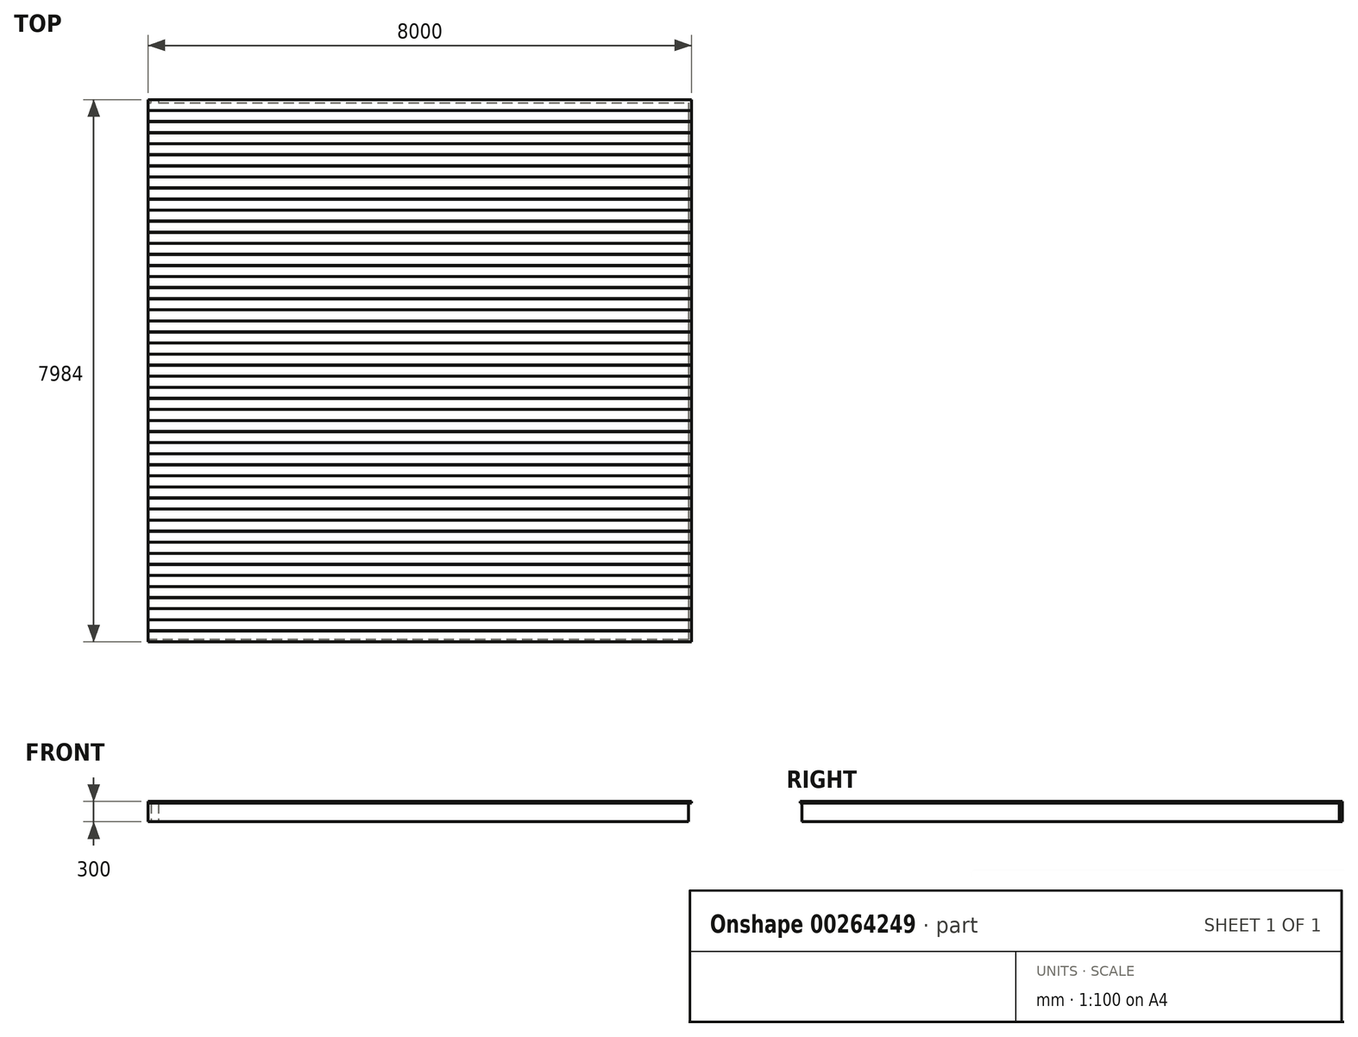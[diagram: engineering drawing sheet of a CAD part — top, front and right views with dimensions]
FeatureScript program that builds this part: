
annotation { "Feature Type Name" : "Feature", "Feature Type Description" : "" }
export const myFeature = defineFeature(function(context is Context, id is Id, definition is map)
    precondition{}
    {
        {
            var Q0;
            Q0=qCreatedBy(makeId("Top.planeOp"),FACE);
            var sketch = newSketch(context, id + "F0", { "sketchPlane" : qUnion([Q0])});
            skLineSegment(sketch, "E0.bottom", {"start": v(0, 0) * mm, "end": v(8000, 0) * mm});
            skLineSegment(sketch, "E0.top", {"start": v(0, -8000) * mm, "end": v(8000, -8000) * mm});
            skLineSegment(sketch, "E0.left", {"start": v(0, 0) * mm, "end": v(0, -8000) * mm});
            skLineSegment(sketch, "E0.right", {"start": v(8000, 0) * mm, "end": v(8000, -8000) * mm});
            skLineSegment(sketch, "E1.bottom", {"start": v(8000, 0) * mm, "end": v(7955, 0) * mm});
            skLineSegment(sketch, "E1.top", {"start": v(8000, -8000) * mm, "end": v(7955, -8000) * mm});
            skLineSegment(sketch, "E1.right", {"start": v(7955, 0) * mm, "end": v(7955, -8000) * mm});
            skLineSegment(sketch, "E2.bottom", {"start": v(7955, -8000) * mm, "end": v(0, -8000) * mm});
            skLineSegment(sketch, "E2.top", {"start": v(7955, -7955) * mm, "end": v(0, -7955) * mm});
            skLineSegment(sketch, "E2.left", {"start": v(7955, -8000) * mm, "end": v(7955, -7955) * mm});
            skLineSegment(sketch, "E2.right", {"start": v(0, -8000) * mm, "end": v(0, -7955) * mm});
            skLineSegment(sketch, "E3.bottom", {"start": v(0, -8000) * mm, "end": v(45, -8000) * mm});
            skLineSegment(sketch, "E3.top", {"start": v(0, 0) * mm, "end": v(45, 0) * mm});
            skLineSegment(sketch, "E3.left", {"start": v(0, -8000) * mm, "end": v(0, 0) * mm});
            skLineSegment(sketch, "E3.right", {"start": v(45, -8000) * mm, "end": v(45, 0) * mm});
            skLineSegment(sketch, "E4.top", {"start": v(0, -45) * mm, "end": v(8000, -45) * mm});
            skLineSegment(sketch, "E4.left", {"start": v(0, 0) * mm, "end": v(0, -45) * mm});
            skLineSegment(sketch, "E4.right", {"start": v(8000, 0) * mm, "end": v(8000, -45) * mm});
            skLineSegment(sketch, "E5.1.0.0", {"start": v(7400, 0) * mm, "end": v(7400, -8000) * mm});
            skLineSegment(sketch, "E5.1.0.1", {"start": v(7355, 0) * mm, "end": v(7355, -8000) * mm});
            skLineSegment(sketch, "E5.1.0.2", {"start": v(7400, 0) * mm, "end": v(7400, -8000) * mm});
            skLineSegment(sketch, "E5.1.0.3", {"start": v(7355, -8000) * mm, "end": v(7355, -7955) * mm});
            skLineSegment(sketch, "E5.1.0.4", {"start": v(7400, -8000) * mm, "end": v(7355, -8000) * mm});
            skLineSegment(sketch, "E5.1.0.5", {"start": v(7400, 0) * mm, "end": v(7355, 0) * mm});
            skLineSegment(sketch, "E5.1.0.6", {"start": v(7400, 0) * mm, "end": v(7400, -45) * mm});
            skLineSegment(sketch, "E5.2.0.0", {"start": v(6800, 0) * mm, "end": v(6800, -8000) * mm});
            skLineSegment(sketch, "E5.2.0.1", {"start": v(6755, 0) * mm, "end": v(6755, -8000) * mm});
            skLineSegment(sketch, "E5.2.0.2", {"start": v(6800, 0) * mm, "end": v(6800, -8000) * mm});
            skLineSegment(sketch, "E5.2.0.3", {"start": v(6755, -8000) * mm, "end": v(6755, -7955) * mm});
            skLineSegment(sketch, "E5.2.0.4", {"start": v(6800, -8000) * mm, "end": v(6755, -8000) * mm});
            skLineSegment(sketch, "E5.2.0.5", {"start": v(6800, 0) * mm, "end": v(6755, 0) * mm});
            skLineSegment(sketch, "E5.2.0.6", {"start": v(6800, 0) * mm, "end": v(6800, -45) * mm});
            skLineSegment(sketch, "E5.3.0.0", {"start": v(6200, 0) * mm, "end": v(6200, -8000) * mm});
            skLineSegment(sketch, "E5.3.0.1", {"start": v(6155, 0) * mm, "end": v(6155, -8000) * mm});
            skLineSegment(sketch, "E5.3.0.2", {"start": v(6200, 0) * mm, "end": v(6200, -8000) * mm});
            skLineSegment(sketch, "E5.3.0.3", {"start": v(6155, -8000) * mm, "end": v(6155, -7955) * mm});
            skLineSegment(sketch, "E5.3.0.4", {"start": v(6200, -8000) * mm, "end": v(6155, -8000) * mm});
            skLineSegment(sketch, "E5.3.0.5", {"start": v(6200, 0) * mm, "end": v(6155, 0) * mm});
            skLineSegment(sketch, "E5.3.0.6", {"start": v(6200, 0) * mm, "end": v(6200, -45) * mm});
            skLineSegment(sketch, "E5.4.0.0", {"start": v(5600, 0) * mm, "end": v(5600, -8000) * mm});
            skLineSegment(sketch, "E5.4.0.1", {"start": v(5555, 0) * mm, "end": v(5555, -8000) * mm});
            skLineSegment(sketch, "E5.4.0.2", {"start": v(5600, 0) * mm, "end": v(5600, -8000) * mm});
            skLineSegment(sketch, "E5.4.0.3", {"start": v(5555, -8000) * mm, "end": v(5555, -7955) * mm});
            skLineSegment(sketch, "E5.4.0.4", {"start": v(5600, -8000) * mm, "end": v(5555, -8000) * mm});
            skLineSegment(sketch, "E5.4.0.5", {"start": v(5600, 0) * mm, "end": v(5555, 0) * mm});
            skLineSegment(sketch, "E5.4.0.6", {"start": v(5600, 0) * mm, "end": v(5600, -45) * mm});
            skLineSegment(sketch, "E5.5.0.0", {"start": v(5000, 0) * mm, "end": v(5000, -8000) * mm});
            skLineSegment(sketch, "E5.5.0.1", {"start": v(4955, 0) * mm, "end": v(4955, -8000) * mm});
            skLineSegment(sketch, "E5.5.0.2", {"start": v(5000, 0) * mm, "end": v(5000, -8000) * mm});
            skLineSegment(sketch, "E5.5.0.3", {"start": v(4955, -8000) * mm, "end": v(4955, -7955) * mm});
            skLineSegment(sketch, "E5.5.0.4", {"start": v(5000, -8000) * mm, "end": v(4955, -8000) * mm});
            skLineSegment(sketch, "E5.5.0.5", {"start": v(5000, 0) * mm, "end": v(4955, 0) * mm});
            skLineSegment(sketch, "E5.5.0.6", {"start": v(5000, 0) * mm, "end": v(5000, -45) * mm});
            skLineSegment(sketch, "E5.6.0.0", {"start": v(4400, 0) * mm, "end": v(4400, -8000) * mm});
            skLineSegment(sketch, "E5.6.0.1", {"start": v(4355, 0) * mm, "end": v(4355, -8000) * mm});
            skLineSegment(sketch, "E5.6.0.2", {"start": v(4400, 0) * mm, "end": v(4400, -8000) * mm});
            skLineSegment(sketch, "E5.6.0.3", {"start": v(4355, -8000) * mm, "end": v(4355, -7955) * mm});
            skLineSegment(sketch, "E5.6.0.4", {"start": v(4400, -8000) * mm, "end": v(4355, -8000) * mm});
            skLineSegment(sketch, "E5.6.0.5", {"start": v(4400, 0) * mm, "end": v(4355, 0) * mm});
            skLineSegment(sketch, "E5.6.0.6", {"start": v(4400, 0) * mm, "end": v(4400, -45) * mm});
            skLineSegment(sketch, "E5.7.0.0", {"start": v(3800, 0) * mm, "end": v(3800, -8000) * mm});
            skLineSegment(sketch, "E5.7.0.1", {"start": v(3755, 0) * mm, "end": v(3755, -8000) * mm});
            skLineSegment(sketch, "E5.7.0.2", {"start": v(3800, 0) * mm, "end": v(3800, -8000) * mm});
            skLineSegment(sketch, "E5.7.0.3", {"start": v(3755, -8000) * mm, "end": v(3755, -7955) * mm});
            skLineSegment(sketch, "E5.7.0.4", {"start": v(3800, -8000) * mm, "end": v(3755, -8000) * mm});
            skLineSegment(sketch, "E5.7.0.5", {"start": v(3800, 0) * mm, "end": v(3755, 0) * mm});
            skLineSegment(sketch, "E5.7.0.6", {"start": v(3800, 0) * mm, "end": v(3800, -45) * mm});
            skLineSegment(sketch, "E5.8.0.0", {"start": v(3200, 0) * mm, "end": v(3200, -8000) * mm});
            skLineSegment(sketch, "E5.8.0.1", {"start": v(3155, 0) * mm, "end": v(3155, -8000) * mm});
            skLineSegment(sketch, "E5.8.0.2", {"start": v(3200, 0) * mm, "end": v(3200, -8000) * mm});
            skLineSegment(sketch, "E5.8.0.3", {"start": v(3155, -8000) * mm, "end": v(3155, -7955) * mm});
            skLineSegment(sketch, "E5.8.0.4", {"start": v(3200, -8000) * mm, "end": v(3155, -8000) * mm});
            skLineSegment(sketch, "E5.8.0.5", {"start": v(3200, 0) * mm, "end": v(3155, 0) * mm});
            skLineSegment(sketch, "E5.8.0.6", {"start": v(3200, 0) * mm, "end": v(3200, -45) * mm});
            skLineSegment(sketch, "E5.9.0.0", {"start": v(2600, 0) * mm, "end": v(2600, -8000) * mm});
            skLineSegment(sketch, "E5.9.0.1", {"start": v(2555, 0) * mm, "end": v(2555, -8000) * mm});
            skLineSegment(sketch, "E5.9.0.2", {"start": v(2600, 0) * mm, "end": v(2600, -8000) * mm});
            skLineSegment(sketch, "E5.9.0.3", {"start": v(2555, -8000) * mm, "end": v(2555, -7955) * mm});
            skLineSegment(sketch, "E5.9.0.4", {"start": v(2600, -8000) * mm, "end": v(2555, -8000) * mm});
            skLineSegment(sketch, "E5.9.0.5", {"start": v(2600, 0) * mm, "end": v(2555, 0) * mm});
            skLineSegment(sketch, "E5.9.0.6", {"start": v(2600, 0) * mm, "end": v(2600, -45) * mm});
            skLineSegment(sketch, "E5.10.0.0", {"start": v(2000, 0) * mm, "end": v(2000, -8000) * mm});
            skLineSegment(sketch, "E5.10.0.1", {"start": v(1955, 0) * mm, "end": v(1955, -8000) * mm});
            skLineSegment(sketch, "E5.10.0.2", {"start": v(2000, 0) * mm, "end": v(2000, -8000) * mm});
            skLineSegment(sketch, "E5.10.0.3", {"start": v(1955, -8000) * mm, "end": v(1955, -7955) * mm});
            skLineSegment(sketch, "E5.10.0.4", {"start": v(2000, -8000) * mm, "end": v(1955, -8000) * mm});
            skLineSegment(sketch, "E5.10.0.5", {"start": v(2000, 0) * mm, "end": v(1955, 0) * mm});
            skLineSegment(sketch, "E5.10.0.6", {"start": v(2000, 0) * mm, "end": v(2000, -45) * mm});
            skLineSegment(sketch, "E5.11.0.0", {"start": v(1400, 0) * mm, "end": v(1400, -8000) * mm});
            skLineSegment(sketch, "E5.11.0.1", {"start": v(1355, 0) * mm, "end": v(1355, -8000) * mm});
            skLineSegment(sketch, "E5.11.0.2", {"start": v(1400, 0) * mm, "end": v(1400, -8000) * mm});
            skLineSegment(sketch, "E5.11.0.3", {"start": v(1355, -8000) * mm, "end": v(1355, -7955) * mm});
            skLineSegment(sketch, "E5.11.0.4", {"start": v(1400, -8000) * mm, "end": v(1355, -8000) * mm});
            skLineSegment(sketch, "E5.11.0.5", {"start": v(1400, 0) * mm, "end": v(1355, 0) * mm});
            skLineSegment(sketch, "E5.11.0.6", {"start": v(1400, 0) * mm, "end": v(1400, -45) * mm});
            skLineSegment(sketch, "E5.12.0.0", {"start": v(800, 0) * mm, "end": v(800, -8000) * mm});
            skLineSegment(sketch, "E5.12.0.1", {"start": v(755, 0) * mm, "end": v(755, -8000) * mm});
            skLineSegment(sketch, "E5.12.0.2", {"start": v(800, 0) * mm, "end": v(800, -8000) * mm});
            skLineSegment(sketch, "E5.12.0.3", {"start": v(755, -8000) * mm, "end": v(755, -7955) * mm});
            skLineSegment(sketch, "E5.12.0.4", {"start": v(800, -8000) * mm, "end": v(755, -8000) * mm});
            skLineSegment(sketch, "E5.12.0.5", {"start": v(800, 0) * mm, "end": v(755, 0) * mm});
            skLineSegment(sketch, "E5.12.0.6", {"start": v(800, 0) * mm, "end": v(800, -45) * mm});
            skLineSegment(sketch, "E5.direction1", {"start": v(7955, -8000) * mm, "end": v(7355, -8000) * mm, "construction": true});
            skLineSegment(sketch, "E6.0.13.0", {"start": v(200, 0) * mm, "end": v(200, -8000) * mm});
            skLineSegment(sketch, "E6.3.13.0", {"start": v(155, 0) * mm, "end": v(155, -8000) * mm});
            skLineSegment(sketch, "E6.6.13.0", {"start": v(200, 0) * mm, "end": v(200, -8000) * mm});
            skLineSegment(sketch, "E6.9.13.0", {"start": v(155, -8000) * mm, "end": v(155, -7955) * mm});
            skLineSegment(sketch, "E6.12.13.0", {"start": v(200, -8000) * mm, "end": v(155, -8000) * mm});
            skLineSegment(sketch, "E6.15.13.0", {"start": v(200, 0) * mm, "end": v(155, 0) * mm});
            skLineSegment(sketch, "E6.18.13.0", {"start": v(200, 0) * mm, "end": v(200, -45) * mm});
            skSolve(sketch);
        }
        {
            var Q0;
            {var subQ5=sQuery(id+"F0.wireOp",EDGE,"E4.right");Q0=makeQuery(id+"F0.imprint","IMPRINT",FACE,{"disambiguationData":[TD([[makeQuery(id+"F0.imprint","IMPRINT",EDGE,{"derivedFrom":subQ5}),-1.0]])]});}
            var Q1;
            {var subQ5=sQuery(id+"F0.wireOp",EDGE,"E3.bottom");Q1=makeQuery(id+"F0.imprint","IMPRINT",FACE,{"disambiguationData":[TD([[makeQuery(id+"F0.imprint","IMPRINT",EDGE,{"derivedFrom":subQ5}),1.0]])]});}
            var Q2;
            {var subQ5=sQuery(id+"F0.wireOp",EDGE,"E4.left");Q2=makeQuery(id+"F0.imprint","IMPRINT",FACE,{"disambiguationData":[TD([[makeQuery(id+"F0.imprint","IMPRINT",EDGE,{"derivedFrom":subQ5}),1.0]])]});}
            var Q3;
            Q3=makeQuery(id+"F0.imprint","IMPRINT",FACE,{"disambiguationData":[TD([[makeQuery(id+"F0.imprint","IMPRINT",EDGE,{"derivedFrom":sQuery(id+"F0.wireOp",EDGE,"E1.top")}),-1.0]])]});
            var Q4;
            {var subQ5=sQuery(id+"F0.wireOp",EDGE,"E5.1.0.6");Q4=makeQuery(id+"F0.imprint","IMPRINT",FACE,{"disambiguationData":[TD([[makeQuery(id+"F0.imprint","IMPRINT",EDGE,{"derivedFrom":subQ5}),1.0]])]});}
            var Q5;
            {var subQ0=sQuery(id+"F0.wireOp",EDGE,"E2.left");Q5=makeQuery(id+"F0.imprint","IMPRINT",FACE,{"disambiguationData":[TD([[makeQuery(id+"F0.imprint","IMPRINT",EDGE,{"derivedFrom":subQ0}),1.0]])]});}
            var Q6;
            {var subQ0=sQuery(id+"F0.wireOp",EDGE,"E5.1.0.3");Q6=makeQuery(id+"F0.imprint","IMPRINT",FACE,{"disambiguationData":[TD([[makeQuery(id+"F0.imprint","IMPRINT",EDGE,{"derivedFrom":subQ0}),1.0]])]});}
            var Q7;
            {var subQ0=sQuery(id+"F0.wireOp",EDGE,"E5.2.0.3");Q7=makeQuery(id+"F0.imprint","IMPRINT",FACE,{"disambiguationData":[TD([[makeQuery(id+"F0.imprint","IMPRINT",EDGE,{"derivedFrom":subQ0}),1.0]])]});}
            var Q8;
            {var subQ0=sQuery(id+"F0.wireOp",EDGE,"E5.3.0.3");Q8=makeQuery(id+"F0.imprint","IMPRINT",FACE,{"disambiguationData":[TD([[makeQuery(id+"F0.imprint","IMPRINT",EDGE,{"derivedFrom":subQ0}),1.0]])]});}
            var Q9;
            {var subQ0=sQuery(id+"F0.wireOp",EDGE,"E5.4.0.3");Q9=makeQuery(id+"F0.imprint","IMPRINT",FACE,{"disambiguationData":[TD([[makeQuery(id+"F0.imprint","IMPRINT",EDGE,{"derivedFrom":subQ0}),1.0]])]});}
            var Q10;
            {var subQ0=sQuery(id+"F0.wireOp",EDGE,"E5.5.0.3");Q10=makeQuery(id+"F0.imprint","IMPRINT",FACE,{"disambiguationData":[TD([[makeQuery(id+"F0.imprint","IMPRINT",EDGE,{"derivedFrom":subQ0}),1.0]])]});}
            var Q11;
            {var subQ0=sQuery(id+"F0.wireOp",EDGE,"E5.6.0.3");Q11=makeQuery(id+"F0.imprint","IMPRINT",FACE,{"disambiguationData":[TD([[makeQuery(id+"F0.imprint","IMPRINT",EDGE,{"derivedFrom":subQ0}),1.0]])]});}
            var Q12;
            {var subQ0=sQuery(id+"F0.wireOp",EDGE,"E5.7.0.3");Q12=makeQuery(id+"F0.imprint","IMPRINT",FACE,{"disambiguationData":[TD([[makeQuery(id+"F0.imprint","IMPRINT",EDGE,{"derivedFrom":subQ0}),1.0]])]});}
            var Q13;
            {var subQ0=sQuery(id+"F0.wireOp",EDGE,"E5.8.0.3");Q13=makeQuery(id+"F0.imprint","IMPRINT",FACE,{"disambiguationData":[TD([[makeQuery(id+"F0.imprint","IMPRINT",EDGE,{"derivedFrom":subQ0}),1.0]])]});}
            var Q14;
            {var subQ0=sQuery(id+"F0.wireOp",EDGE,"E5.9.0.3");Q14=makeQuery(id+"F0.imprint","IMPRINT",FACE,{"disambiguationData":[TD([[makeQuery(id+"F0.imprint","IMPRINT",EDGE,{"derivedFrom":subQ0}),1.0]])]});}
            var Q15;
            {var subQ0=sQuery(id+"F0.wireOp",EDGE,"E5.10.0.3");Q15=makeQuery(id+"F0.imprint","IMPRINT",FACE,{"disambiguationData":[TD([[makeQuery(id+"F0.imprint","IMPRINT",EDGE,{"derivedFrom":subQ0}),1.0]])]});}
            var Q16;
            {var subQ0=sQuery(id+"F0.wireOp",EDGE,"E5.11.0.3");Q16=makeQuery(id+"F0.imprint","IMPRINT",FACE,{"disambiguationData":[TD([[makeQuery(id+"F0.imprint","IMPRINT",EDGE,{"derivedFrom":subQ0}),1.0]])]});}
            var Q17;
            {var subQ0=sQuery(id+"F0.wireOp",EDGE,"E5.12.0.3");Q17=makeQuery(id+"F0.imprint","IMPRINT",FACE,{"disambiguationData":[TD([[makeQuery(id+"F0.imprint","IMPRINT",EDGE,{"derivedFrom":subQ0}),1.0]])]});}
            var Q18;
            {var subQ3=sQuery(id+"F0.wireOp",EDGE,"E5.13.0.3");Q18=makeQuery(id+"F0.imprint","IMPRINT",FACE,{"disambiguationData":[TD([[makeQuery(id+"F0.imprint","IMPRINT",EDGE,{"derivedFrom":subQ3}),1.0]])]});}
            var Q19;
            {var subQ0=sQuery(id+"F0.wireOp",EDGE,"E5.1.0.3");Q19=makeQuery(id+"F0.imprint","IMPRINT",FACE,{"disambiguationData":[TD([[makeQuery(id+"F0.imprint","IMPRINT",EDGE,{"derivedFrom":subQ0}),-1.0]])]});}
            var Q20;
            {var subQ0=sQuery(id+"F0.wireOp",EDGE,"E5.2.0.3");Q20=makeQuery(id+"F0.imprint","IMPRINT",FACE,{"disambiguationData":[TD([[makeQuery(id+"F0.imprint","IMPRINT",EDGE,{"derivedFrom":subQ0}),-1.0]])]});}
            var Q21;
            {var subQ0=sQuery(id+"F0.wireOp",EDGE,"E5.3.0.3");Q21=makeQuery(id+"F0.imprint","IMPRINT",FACE,{"disambiguationData":[TD([[makeQuery(id+"F0.imprint","IMPRINT",EDGE,{"derivedFrom":subQ0}),-1.0]])]});}
            var Q22;
            {var subQ0=sQuery(id+"F0.wireOp",EDGE,"E5.4.0.3");Q22=makeQuery(id+"F0.imprint","IMPRINT",FACE,{"disambiguationData":[TD([[makeQuery(id+"F0.imprint","IMPRINT",EDGE,{"derivedFrom":subQ0}),-1.0]])]});}
            var Q23;
            {var subQ0=sQuery(id+"F0.wireOp",EDGE,"E5.5.0.3");Q23=makeQuery(id+"F0.imprint","IMPRINT",FACE,{"disambiguationData":[TD([[makeQuery(id+"F0.imprint","IMPRINT",EDGE,{"derivedFrom":subQ0}),-1.0]])]});}
            var Q24;
            {var subQ0=sQuery(id+"F0.wireOp",EDGE,"E5.6.0.3");Q24=makeQuery(id+"F0.imprint","IMPRINT",FACE,{"disambiguationData":[TD([[makeQuery(id+"F0.imprint","IMPRINT",EDGE,{"derivedFrom":subQ0}),-1.0]])]});}
            var Q25;
            {var subQ0=sQuery(id+"F0.wireOp",EDGE,"E5.7.0.3");Q25=makeQuery(id+"F0.imprint","IMPRINT",FACE,{"disambiguationData":[TD([[makeQuery(id+"F0.imprint","IMPRINT",EDGE,{"derivedFrom":subQ0}),-1.0]])]});}
            var Q26;
            {var subQ0=sQuery(id+"F0.wireOp",EDGE,"E5.8.0.3");Q26=makeQuery(id+"F0.imprint","IMPRINT",FACE,{"disambiguationData":[TD([[makeQuery(id+"F0.imprint","IMPRINT",EDGE,{"derivedFrom":subQ0}),-1.0]])]});}
            var Q27;
            {var subQ0=sQuery(id+"F0.wireOp",EDGE,"E5.9.0.3");Q27=makeQuery(id+"F0.imprint","IMPRINT",FACE,{"disambiguationData":[TD([[makeQuery(id+"F0.imprint","IMPRINT",EDGE,{"derivedFrom":subQ0}),-1.0]])]});}
            var Q28;
            {var subQ0=sQuery(id+"F0.wireOp",EDGE,"E5.10.0.3");Q28=makeQuery(id+"F0.imprint","IMPRINT",FACE,{"disambiguationData":[TD([[makeQuery(id+"F0.imprint","IMPRINT",EDGE,{"derivedFrom":subQ0}),-1.0]])]});}
            var Q29;
            {var subQ0=sQuery(id+"F0.wireOp",EDGE,"E5.11.0.3");Q29=makeQuery(id+"F0.imprint","IMPRINT",FACE,{"disambiguationData":[TD([[makeQuery(id+"F0.imprint","IMPRINT",EDGE,{"derivedFrom":subQ0}),-1.0]])]});}
            var Q30;
            {var subQ0=sQuery(id+"F0.wireOp",EDGE,"E5.12.0.3");Q30=makeQuery(id+"F0.imprint","IMPRINT",FACE,{"disambiguationData":[TD([[makeQuery(id+"F0.imprint","IMPRINT",EDGE,{"derivedFrom":subQ0}),-1.0]])]});}
            var Q31;
            {var subQ0=sQuery(id+"F0.wireOp",EDGE,"E5.13.0.3");Q31=makeQuery(id+"F0.imprint","IMPRINT",FACE,{"disambiguationData":[TD([[makeQuery(id+"F0.imprint","IMPRINT",EDGE,{"derivedFrom":subQ0}),-1.0]])]});}
            var Q32;
            {var subQ0=sQuery(id+"F0.wireOp",EDGE,"E3.left");var subQ1=sQuery(id+"F0.wireOp",EDGE,"E2.top");var subQ2=makeQuery(id+"F0.imprint","INTERSECT",VERTEX,{"derivedFrom":[subQ1,subQ0]});Q32=makeQuery(id+"F0.imprint","IMPRINT",FACE,{"disambiguationData":[TD([[makeQuery(id+"F0.imprint","IMPRINT",EDGE,{"disambiguationData":[TD([[subQ2,1.0]])],"derivedFrom":subQ1}),-1.0]])]});}
            var Q33;
            {var subQ0=sQuery(id+"F0.wireOp",EDGE,"E0.bottom");var subQ1=sQuery(id+"F0.wireOp",EDGE,"E3.right");var subQ2=makeQuery(id+"F0.imprint","INTERSECT",VERTEX,{"derivedFrom":[subQ1,subQ0]});Q33=makeQuery(id+"F0.imprint","IMPRINT",FACE,{"disambiguationData":[TD([[makeQuery(id+"F0.imprint","IMPRINT",EDGE,{"disambiguationData":[TD([[subQ2,1.0]])],"derivedFrom":subQ1}),-1.0]])]});}
            var Q34;
            {var subQ3=sQuery(id+"F0.wireOp",EDGE,"E5.13.0.6");Q34=makeQuery(id+"F0.imprint","IMPRINT",FACE,{"disambiguationData":[TD([[makeQuery(id+"F0.imprint","IMPRINT",EDGE,{"derivedFrom":subQ3}),1.0]])]});}
            var Q35;
            {var subQ3=sQuery(id+"F0.wireOp",EDGE,"E5.12.0.6");Q35=makeQuery(id+"F0.imprint","IMPRINT",FACE,{"disambiguationData":[TD([[makeQuery(id+"F0.imprint","IMPRINT",EDGE,{"derivedFrom":subQ3}),1.0]])]});}
            var Q36;
            {var subQ3=sQuery(id+"F0.wireOp",EDGE,"E5.11.0.6");Q36=makeQuery(id+"F0.imprint","IMPRINT",FACE,{"disambiguationData":[TD([[makeQuery(id+"F0.imprint","IMPRINT",EDGE,{"derivedFrom":subQ3}),1.0]])]});}
            var Q37;
            {var subQ3=sQuery(id+"F0.wireOp",EDGE,"E5.10.0.6");Q37=makeQuery(id+"F0.imprint","IMPRINT",FACE,{"disambiguationData":[TD([[makeQuery(id+"F0.imprint","IMPRINT",EDGE,{"derivedFrom":subQ3}),1.0]])]});}
            var Q38;
            {var subQ3=sQuery(id+"F0.wireOp",EDGE,"E5.9.0.6");Q38=makeQuery(id+"F0.imprint","IMPRINT",FACE,{"disambiguationData":[TD([[makeQuery(id+"F0.imprint","IMPRINT",EDGE,{"derivedFrom":subQ3}),1.0]])]});}
            var Q39;
            {var subQ3=sQuery(id+"F0.wireOp",EDGE,"E5.8.0.6");Q39=makeQuery(id+"F0.imprint","IMPRINT",FACE,{"disambiguationData":[TD([[makeQuery(id+"F0.imprint","IMPRINT",EDGE,{"derivedFrom":subQ3}),1.0]])]});}
            var Q40;
            {var subQ3=sQuery(id+"F0.wireOp",EDGE,"E5.7.0.6");Q40=makeQuery(id+"F0.imprint","IMPRINT",FACE,{"disambiguationData":[TD([[makeQuery(id+"F0.imprint","IMPRINT",EDGE,{"derivedFrom":subQ3}),1.0]])]});}
            var Q41;
            {var subQ3=sQuery(id+"F0.wireOp",EDGE,"E5.6.0.6");Q41=makeQuery(id+"F0.imprint","IMPRINT",FACE,{"disambiguationData":[TD([[makeQuery(id+"F0.imprint","IMPRINT",EDGE,{"derivedFrom":subQ3}),1.0]])]});}
            var Q42;
            {var subQ3=sQuery(id+"F0.wireOp",EDGE,"E5.5.0.6");Q42=makeQuery(id+"F0.imprint","IMPRINT",FACE,{"disambiguationData":[TD([[makeQuery(id+"F0.imprint","IMPRINT",EDGE,{"derivedFrom":subQ3}),1.0]])]});}
            var Q43;
            {var subQ3=sQuery(id+"F0.wireOp",EDGE,"E5.4.0.6");Q43=makeQuery(id+"F0.imprint","IMPRINT",FACE,{"disambiguationData":[TD([[makeQuery(id+"F0.imprint","IMPRINT",EDGE,{"derivedFrom":subQ3}),1.0]])]});}
            var Q44;
            {var subQ3=sQuery(id+"F0.wireOp",EDGE,"E5.3.0.6");Q44=makeQuery(id+"F0.imprint","IMPRINT",FACE,{"disambiguationData":[TD([[makeQuery(id+"F0.imprint","IMPRINT",EDGE,{"derivedFrom":subQ3}),1.0]])]});}
            var Q45;
            {var subQ3=sQuery(id+"F0.wireOp",EDGE,"E5.2.0.6");Q45=makeQuery(id+"F0.imprint","IMPRINT",FACE,{"disambiguationData":[TD([[makeQuery(id+"F0.imprint","IMPRINT",EDGE,{"derivedFrom":subQ3}),1.0]])]});}
            var Q46;
            {var subQ4=sQuery(id+"F0.wireOp",EDGE,"E5.13.0.5");Q46=makeQuery(id+"F0.imprint","IMPRINT",FACE,{"disambiguationData":[TD([[makeQuery(id+"F0.imprint","IMPRINT",EDGE,{"derivedFrom":subQ4}),1.0]])]});}
            var Q47;
            {var subQ4=sQuery(id+"F0.wireOp",EDGE,"E5.12.0.5");Q47=makeQuery(id+"F0.imprint","IMPRINT",FACE,{"disambiguationData":[TD([[makeQuery(id+"F0.imprint","IMPRINT",EDGE,{"derivedFrom":subQ4}),1.0]])]});}
            var Q48;
            {var subQ4=sQuery(id+"F0.wireOp",EDGE,"E5.11.0.5");Q48=makeQuery(id+"F0.imprint","IMPRINT",FACE,{"disambiguationData":[TD([[makeQuery(id+"F0.imprint","IMPRINT",EDGE,{"derivedFrom":subQ4}),1.0]])]});}
            var Q49;
            {var subQ4=sQuery(id+"F0.wireOp",EDGE,"E5.10.0.5");Q49=makeQuery(id+"F0.imprint","IMPRINT",FACE,{"disambiguationData":[TD([[makeQuery(id+"F0.imprint","IMPRINT",EDGE,{"derivedFrom":subQ4}),1.0]])]});}
            var Q50;
            {var subQ4=sQuery(id+"F0.wireOp",EDGE,"E5.9.0.5");Q50=makeQuery(id+"F0.imprint","IMPRINT",FACE,{"disambiguationData":[TD([[makeQuery(id+"F0.imprint","IMPRINT",EDGE,{"derivedFrom":subQ4}),1.0]])]});}
            var Q51;
            {var subQ4=sQuery(id+"F0.wireOp",EDGE,"E5.8.0.5");Q51=makeQuery(id+"F0.imprint","IMPRINT",FACE,{"disambiguationData":[TD([[makeQuery(id+"F0.imprint","IMPRINT",EDGE,{"derivedFrom":subQ4}),1.0]])]});}
            var Q52;
            {var subQ4=sQuery(id+"F0.wireOp",EDGE,"E5.7.0.5");Q52=makeQuery(id+"F0.imprint","IMPRINT",FACE,{"disambiguationData":[TD([[makeQuery(id+"F0.imprint","IMPRINT",EDGE,{"derivedFrom":subQ4}),1.0]])]});}
            var Q53;
            {var subQ4=sQuery(id+"F0.wireOp",EDGE,"E5.6.0.5");Q53=makeQuery(id+"F0.imprint","IMPRINT",FACE,{"disambiguationData":[TD([[makeQuery(id+"F0.imprint","IMPRINT",EDGE,{"derivedFrom":subQ4}),1.0]])]});}
            var Q54;
            {var subQ4=sQuery(id+"F0.wireOp",EDGE,"E5.5.0.5");Q54=makeQuery(id+"F0.imprint","IMPRINT",FACE,{"disambiguationData":[TD([[makeQuery(id+"F0.imprint","IMPRINT",EDGE,{"derivedFrom":subQ4}),1.0]])]});}
            var Q55;
            {var subQ4=sQuery(id+"F0.wireOp",EDGE,"E5.4.0.5");Q55=makeQuery(id+"F0.imprint","IMPRINT",FACE,{"disambiguationData":[TD([[makeQuery(id+"F0.imprint","IMPRINT",EDGE,{"derivedFrom":subQ4}),1.0]])]});}
            var Q56;
            {var subQ4=sQuery(id+"F0.wireOp",EDGE,"E5.3.0.5");Q56=makeQuery(id+"F0.imprint","IMPRINT",FACE,{"disambiguationData":[TD([[makeQuery(id+"F0.imprint","IMPRINT",EDGE,{"derivedFrom":subQ4}),1.0]])]});}
            var Q57;
            {var subQ4=sQuery(id+"F0.wireOp",EDGE,"E5.2.0.5");Q57=makeQuery(id+"F0.imprint","IMPRINT",FACE,{"disambiguationData":[TD([[makeQuery(id+"F0.imprint","IMPRINT",EDGE,{"derivedFrom":subQ4}),1.0]])]});}
            var Q58;
            {var subQ4=sQuery(id+"F0.wireOp",EDGE,"E5.1.0.5");Q58=makeQuery(id+"F0.imprint","IMPRINT",FACE,{"disambiguationData":[TD([[makeQuery(id+"F0.imprint","IMPRINT",EDGE,{"derivedFrom":subQ4}),1.0]])]});}
            var Q59;
            {var subQ1=sQuery(id+"F0.wireOp",EDGE,"E2.top");var subQ3=sQuery(id+"F0.wireOp",EDGE,"E5.13.0.2");var subQ4=makeQuery(id+"F0.imprint","INTERSECT",VERTEX,{"derivedFrom":[subQ1,subQ3]});Q59=makeQuery(id+"F0.imprint","IMPRINT",FACE,{"disambiguationData":[TD([[makeQuery(id+"F0.imprint","IMPRINT",EDGE,{"disambiguationData":[TD([[subQ4,-1.0]])],"derivedFrom":subQ1}),-1.0]])]});}
            var Q60;
            {var subQ1=sQuery(id+"F0.wireOp",EDGE,"E2.top");var subQ3=sQuery(id+"F0.wireOp",EDGE,"E5.12.0.2");var subQ4=makeQuery(id+"F0.imprint","INTERSECT",VERTEX,{"derivedFrom":[subQ1,subQ3]});Q60=makeQuery(id+"F0.imprint","IMPRINT",FACE,{"disambiguationData":[TD([[makeQuery(id+"F0.imprint","IMPRINT",EDGE,{"disambiguationData":[TD([[subQ4,-1.0]])],"derivedFrom":subQ1}),-1.0]])]});}
            var Q61;
            {var subQ1=sQuery(id+"F0.wireOp",EDGE,"E2.top");var subQ3=sQuery(id+"F0.wireOp",EDGE,"E5.8.0.2");var subQ4=makeQuery(id+"F0.imprint","INTERSECT",VERTEX,{"derivedFrom":[subQ1,subQ3]});Q61=makeQuery(id+"F0.imprint","IMPRINT",FACE,{"disambiguationData":[TD([[makeQuery(id+"F0.imprint","IMPRINT",EDGE,{"disambiguationData":[TD([[subQ4,-1.0]])],"derivedFrom":subQ1}),-1.0]])]});}
            var Q62;
            {var subQ1=sQuery(id+"F0.wireOp",EDGE,"E2.top");var subQ3=sQuery(id+"F0.wireOp",EDGE,"E5.2.0.2");var subQ4=makeQuery(id+"F0.imprint","INTERSECT",VERTEX,{"derivedFrom":[subQ1,subQ3]});Q62=makeQuery(id+"F0.imprint","IMPRINT",FACE,{"disambiguationData":[TD([[makeQuery(id+"F0.imprint","IMPRINT",EDGE,{"disambiguationData":[TD([[subQ4,-1.0]])],"derivedFrom":subQ1}),-1.0]])]});}
            var Q63;
            {var subQ1=sQuery(id+"F0.wireOp",EDGE,"E2.top");var subQ3=sQuery(id+"F0.wireOp",EDGE,"E5.10.0.2");var subQ4=makeQuery(id+"F0.imprint","INTERSECT",VERTEX,{"derivedFrom":[subQ1,subQ3]});Q63=makeQuery(id+"F0.imprint","IMPRINT",FACE,{"disambiguationData":[TD([[makeQuery(id+"F0.imprint","IMPRINT",EDGE,{"disambiguationData":[TD([[subQ4,-1.0]])],"derivedFrom":subQ1}),-1.0]])]});}
            var Q64;
            {var subQ1=sQuery(id+"F0.wireOp",EDGE,"E2.top");var subQ3=sQuery(id+"F0.wireOp",EDGE,"E5.1.0.2");var subQ4=makeQuery(id+"F0.imprint","INTERSECT",VERTEX,{"derivedFrom":[subQ1,subQ3]});Q64=makeQuery(id+"F0.imprint","IMPRINT",FACE,{"disambiguationData":[TD([[makeQuery(id+"F0.imprint","IMPRINT",EDGE,{"disambiguationData":[TD([[subQ4,-1.0]])],"derivedFrom":subQ1}),-1.0]])]});}
            var Q65;
            {var subQ1=sQuery(id+"F0.wireOp",EDGE,"E2.top");var subQ3=sQuery(id+"F0.wireOp",EDGE,"E5.9.0.2");var subQ4=makeQuery(id+"F0.imprint","INTERSECT",VERTEX,{"derivedFrom":[subQ1,subQ3]});Q65=makeQuery(id+"F0.imprint","IMPRINT",FACE,{"disambiguationData":[TD([[makeQuery(id+"F0.imprint","IMPRINT",EDGE,{"disambiguationData":[TD([[subQ4,-1.0]])],"derivedFrom":subQ1}),-1.0]])]});}
            var Q66;
            {var subQ1=sQuery(id+"F0.wireOp",EDGE,"E2.top");var subQ3=sQuery(id+"F0.wireOp",EDGE,"E5.11.0.2");var subQ4=makeQuery(id+"F0.imprint","INTERSECT",VERTEX,{"derivedFrom":[subQ1,subQ3]});Q66=makeQuery(id+"F0.imprint","IMPRINT",FACE,{"disambiguationData":[TD([[makeQuery(id+"F0.imprint","IMPRINT",EDGE,{"disambiguationData":[TD([[subQ4,-1.0]])],"derivedFrom":subQ1}),-1.0]])]});}
            var Q67;
            {var subQ1=sQuery(id+"F0.wireOp",EDGE,"E2.top");var subQ3=sQuery(id+"F0.wireOp",EDGE,"E5.3.0.2");var subQ4=makeQuery(id+"F0.imprint","INTERSECT",VERTEX,{"derivedFrom":[subQ1,subQ3]});Q67=makeQuery(id+"F0.imprint","IMPRINT",FACE,{"disambiguationData":[TD([[makeQuery(id+"F0.imprint","IMPRINT",EDGE,{"disambiguationData":[TD([[subQ4,-1.0]])],"derivedFrom":subQ1}),-1.0]])]});}
            var Q68;
            {var subQ1=sQuery(id+"F0.wireOp",EDGE,"E2.top");var subQ3=sQuery(id+"F0.wireOp",EDGE,"E5.4.0.2");var subQ4=makeQuery(id+"F0.imprint","INTERSECT",VERTEX,{"derivedFrom":[subQ1,subQ3]});Q68=makeQuery(id+"F0.imprint","IMPRINT",FACE,{"disambiguationData":[TD([[makeQuery(id+"F0.imprint","IMPRINT",EDGE,{"disambiguationData":[TD([[subQ4,-1.0]])],"derivedFrom":subQ1}),-1.0]])]});}
            var Q69;
            {var subQ1=sQuery(id+"F0.wireOp",EDGE,"E2.top");var subQ3=sQuery(id+"F0.wireOp",EDGE,"E5.5.0.2");var subQ4=makeQuery(id+"F0.imprint","INTERSECT",VERTEX,{"derivedFrom":[subQ1,subQ3]});Q69=makeQuery(id+"F0.imprint","IMPRINT",FACE,{"disambiguationData":[TD([[makeQuery(id+"F0.imprint","IMPRINT",EDGE,{"disambiguationData":[TD([[subQ4,-1.0]])],"derivedFrom":subQ1}),-1.0]])]});}
            var Q70;
            {var subQ1=sQuery(id+"F0.wireOp",EDGE,"E2.top");var subQ3=sQuery(id+"F0.wireOp",EDGE,"E5.6.0.2");var subQ4=makeQuery(id+"F0.imprint","INTERSECT",VERTEX,{"derivedFrom":[subQ1,subQ3]});Q70=makeQuery(id+"F0.imprint","IMPRINT",FACE,{"disambiguationData":[TD([[makeQuery(id+"F0.imprint","IMPRINT",EDGE,{"disambiguationData":[TD([[subQ4,-1.0]])],"derivedFrom":subQ1}),-1.0]])]});}
            var Q71;
            {var subQ1=sQuery(id+"F0.wireOp",EDGE,"E2.top");var subQ3=sQuery(id+"F0.wireOp",EDGE,"E5.7.0.2");var subQ4=makeQuery(id+"F0.imprint","INTERSECT",VERTEX,{"derivedFrom":[subQ1,subQ3]});Q71=makeQuery(id+"F0.imprint","IMPRINT",FACE,{"disambiguationData":[TD([[makeQuery(id+"F0.imprint","IMPRINT",EDGE,{"disambiguationData":[TD([[subQ4,-1.0]])],"derivedFrom":subQ1}),-1.0]])]});}
            var Q72;
            {var subQ3=sQuery(id+"F0.wireOp",EDGE,"E6.18.13.0");Q72=makeQuery(id+"F0.imprint","IMPRINT",FACE,{"disambiguationData":[TD([[makeQuery(id+"F0.imprint","IMPRINT",EDGE,{"derivedFrom":subQ3}),1.0]])]});}
            var Q73;
            {var subQ4=sQuery(id+"F0.wireOp",EDGE,"E6.15.13.0");Q73=makeQuery(id+"F0.imprint","IMPRINT",FACE,{"disambiguationData":[TD([[makeQuery(id+"F0.imprint","IMPRINT",EDGE,{"derivedFrom":subQ4}),1.0]])]});}
            var Q74;
            {var subQ3=sQuery(id+"F0.wireOp",EDGE,"E6.9.13.0");Q74=makeQuery(id+"F0.imprint","IMPRINT",FACE,{"disambiguationData":[TD([[makeQuery(id+"F0.imprint","IMPRINT",EDGE,{"derivedFrom":subQ3}),1.0]])]});}
            var Q75;
            {var subQ0=sQuery(id+"F0.wireOp",EDGE,"E6.9.13.0");Q75=makeQuery(id+"F0.imprint","IMPRINT",FACE,{"disambiguationData":[TD([[makeQuery(id+"F0.imprint","IMPRINT",EDGE,{"derivedFrom":subQ0}),-1.0]])]});}
            extrude(context, id + "F1", {"entities" : qUnion([Q0, Q1, Q2, Q3, Q4, Q5, Q6, Q7, Q8, Q9, Q10, Q11, Q12, Q13, Q14, Q15, Q16, Q17, Q18, Q19, Q20, Q21, Q22, Q23, Q24, Q25, Q26, Q27, Q28, Q29, Q30, Q31, Q32, Q33, Q34, Q35, Q36, Q37, Q38, Q39, Q40, Q41, Q42, Q43, Q44, Q45, Q46, Q47, Q48, Q49, Q50, Q51, Q52, Q53, Q54, Q55, Q56, Q57, Q58, Q59, Q60, Q61, Q62, Q63, Q64, Q65, Q66, Q67, Q68, Q69, Q70, Q71, Q72, Q73, Q74, Q75]), "depth" : 275 * mm, "offsetDistance" : 25 * mm});
        }
        {
            var Q0;
            Q0=makeQuery(id+"F1.opExtrude","CAP_FACE",FACE,{"disambiguationData":[OSD([sQuery(id+"F0.wireOp",EDGE,"E1.top"),sQuery(id+"F0.wireOp",EDGE,"E0.right"),sQuery(id+"F0.wireOp",EDGE,"E1.right"),sQuery(id+"F0.wireOp",EDGE,"E2.bottom"),sQuery(id+"F0.wireOp",EDGE,"E2.top"),sQuery(id+"F0.wireOp",EDGE,"E3.bottom"),sQuery(id+"F0.wireOp",EDGE,"E3.left"),sQuery(id+"F0.wireOp",EDGE,"E3.right"),sQuery(id+"F0.wireOp",EDGE,"E0.bottom"),sQuery(id+"F0.wireOp",EDGE,"E4.top"),sQuery(id+"F0.wireOp",EDGE,"E4.left"),sQuery(id+"F0.wireOp",EDGE,"E4.right"),sQuery(id+"F0.wireOp",EDGE,"E5.1.0.1"),sQuery(id+"F0.wireOp",EDGE,"E5.1.0.2"),sQuery(id+"F0.wireOp",EDGE,"E5.1.0.4"),sQuery(id+"F0.wireOp",EDGE,"E5.1.0.5"),sQuery(id+"F0.wireOp",EDGE,"E5.2.0.1"),sQuery(id+"F0.wireOp",EDGE,"E5.2.0.2"),sQuery(id+"F0.wireOp",EDGE,"E5.2.0.4"),sQuery(id+"F0.wireOp",EDGE,"E5.2.0.5"),sQuery(id+"F0.wireOp",EDGE,"E5.3.0.1"),sQuery(id+"F0.wireOp",EDGE,"E5.3.0.2"),sQuery(id+"F0.wireOp",EDGE,"E5.3.0.4"),sQuery(id+"F0.wireOp",EDGE,"E5.3.0.5"),sQuery(id+"F0.wireOp",EDGE,"E5.4.0.1"),sQuery(id+"F0.wireOp",EDGE,"E5.4.0.2"),sQuery(id+"F0.wireOp",EDGE,"E5.4.0.4"),sQuery(id+"F0.wireOp",EDGE,"E5.4.0.5"),sQuery(id+"F0.wireOp",EDGE,"E5.5.0.1"),sQuery(id+"F0.wireOp",EDGE,"E5.5.0.2"),sQuery(id+"F0.wireOp",EDGE,"E5.5.0.4"),sQuery(id+"F0.wireOp",EDGE,"E5.5.0.5"),sQuery(id+"F0.wireOp",EDGE,"E5.6.0.1"),sQuery(id+"F0.wireOp",EDGE,"E5.6.0.2"),sQuery(id+"F0.wireOp",EDGE,"E5.6.0.4"),sQuery(id+"F0.wireOp",EDGE,"E5.6.0.5"),sQuery(id+"F0.wireOp",EDGE,"E5.7.0.1"),sQuery(id+"F0.wireOp",EDGE,"E5.7.0.2"),sQuery(id+"F0.wireOp",EDGE,"E5.7.0.4"),sQuery(id+"F0.wireOp",EDGE,"E5.7.0.5"),sQuery(id+"F0.wireOp",EDGE,"E5.8.0.1"),sQuery(id+"F0.wireOp",EDGE,"E5.8.0.2"),sQuery(id+"F0.wireOp",EDGE,"E5.8.0.4"),sQuery(id+"F0.wireOp",EDGE,"E5.8.0.5"),sQuery(id+"F0.wireOp",EDGE,"E5.9.0.1"),sQuery(id+"F0.wireOp",EDGE,"E5.9.0.2"),sQuery(id+"F0.wireOp",EDGE,"E5.9.0.4"),sQuery(id+"F0.wireOp",EDGE,"E5.9.0.5"),sQuery(id+"F0.wireOp",EDGE,"E5.10.0.1"),sQuery(id+"F0.wireOp",EDGE,"E5.10.0.2"),sQuery(id+"F0.wireOp",EDGE,"E5.10.0.4"),sQuery(id+"F0.wireOp",EDGE,"E5.10.0.5"),sQuery(id+"F0.wireOp",EDGE,"E5.11.0.1"),sQuery(id+"F0.wireOp",EDGE,"E5.11.0.2"),sQuery(id+"F0.wireOp",EDGE,"E5.11.0.4"),sQuery(id+"F0.wireOp",EDGE,"E5.11.0.5"),sQuery(id+"F0.wireOp",EDGE,"E5.12.0.1"),sQuery(id+"F0.wireOp",EDGE,"E5.12.0.2"),sQuery(id+"F0.wireOp",EDGE,"E5.12.0.4"),sQuery(id+"F0.wireOp",EDGE,"E5.12.0.5"),sQuery(id+"F0.wireOp",EDGE,"E5.13.0.1"),sQuery(id+"F0.wireOp",EDGE,"E5.13.0.2"),sQuery(id+"F0.wireOp",EDGE,"E5.13.0.4"),sQuery(id+"F0.wireOp",EDGE,"E5.13.0.5")])],"isStart":false});
            var sketch = newSketch(context, id + "F2", { "sketchPlane" : qUnion([Q0])});
            skLineSegment(sketch, "E7.bottom", {"start": v(0, 0) * mm, "end": v(8000, 0) * mm});
            skLineSegment(sketch, "E7.top", {"start": v(0, -160) * mm, "end": v(8000, -160) * mm});
            skLineSegment(sketch, "E7.left", {"start": v(0, 0) * mm, "end": v(0, -160) * mm});
            skLineSegment(sketch, "E7.right", {"start": v(8000, 0) * mm, "end": v(8000, -160) * mm});
            skLineSegment(sketch, "E8.0.1.0", {"start": v(0, -163) * mm, "end": v(8000, -163) * mm});
            skLineSegment(sketch, "E8.0.1.1", {"start": v(0, -323) * mm, "end": v(8000, -323) * mm});
            skLineSegment(sketch, "E8.0.1.2", {"start": v(8000, -163) * mm, "end": v(8000, -323) * mm});
            skLineSegment(sketch, "E8.0.1.3", {"start": v(0, -163) * mm, "end": v(0, -323) * mm});
            skLineSegment(sketch, "E8.0.2.0", {"start": v(0, -326) * mm, "end": v(8000, -326) * mm});
            skLineSegment(sketch, "E8.0.2.1", {"start": v(0, -486) * mm, "end": v(8000, -486) * mm});
            skLineSegment(sketch, "E8.0.2.2", {"start": v(8000, -326) * mm, "end": v(8000, -486) * mm});
            skLineSegment(sketch, "E8.0.2.3", {"start": v(0, -326) * mm, "end": v(0, -486) * mm});
            skLineSegment(sketch, "E8.0.3.0", {"start": v(0, -489) * mm, "end": v(8000, -489) * mm});
            skLineSegment(sketch, "E8.0.3.1", {"start": v(0, -649) * mm, "end": v(8000, -649) * mm});
            skLineSegment(sketch, "E8.0.3.2", {"start": v(8000, -489) * mm, "end": v(8000, -649) * mm});
            skLineSegment(sketch, "E8.0.3.3", {"start": v(0, -489) * mm, "end": v(0, -649) * mm});
            skLineSegment(sketch, "E8.0.4.0", {"start": v(0, -652) * mm, "end": v(8000, -652) * mm});
            skLineSegment(sketch, "E8.0.4.1", {"start": v(0, -812) * mm, "end": v(8000, -812) * mm});
            skLineSegment(sketch, "E8.0.4.2", {"start": v(8000, -652) * mm, "end": v(8000, -812) * mm});
            skLineSegment(sketch, "E8.0.4.3", {"start": v(0, -652) * mm, "end": v(0, -812) * mm});
            skLineSegment(sketch, "E8.0.5.0", {"start": v(0, -815) * mm, "end": v(8000, -815) * mm});
            skLineSegment(sketch, "E8.0.5.1", {"start": v(0, -975) * mm, "end": v(8000, -975) * mm});
            skLineSegment(sketch, "E8.0.5.2", {"start": v(8000, -815) * mm, "end": v(8000, -975) * mm});
            skLineSegment(sketch, "E8.0.5.3", {"start": v(0, -815) * mm, "end": v(0, -975) * mm});
            skLineSegment(sketch, "E8.0.6.0", {"start": v(0, -978) * mm, "end": v(8000, -978) * mm});
            skLineSegment(sketch, "E8.0.6.1", {"start": v(0, -1138) * mm, "end": v(8000, -1138) * mm});
            skLineSegment(sketch, "E8.0.6.2", {"start": v(8000, -978) * mm, "end": v(8000, -1138) * mm});
            skLineSegment(sketch, "E8.0.6.3", {"start": v(0, -978) * mm, "end": v(0, -1138) * mm});
            skLineSegment(sketch, "E8.0.7.0", {"start": v(0, -1141) * mm, "end": v(8000, -1141) * mm});
            skLineSegment(sketch, "E8.0.7.1", {"start": v(0, -1301) * mm, "end": v(8000, -1301) * mm});
            skLineSegment(sketch, "E8.0.7.2", {"start": v(8000, -1141) * mm, "end": v(8000, -1301) * mm});
            skLineSegment(sketch, "E8.0.7.3", {"start": v(0, -1141) * mm, "end": v(0, -1301) * mm});
            skLineSegment(sketch, "E8.0.8.0", {"start": v(0, -1304) * mm, "end": v(8000, -1304) * mm});
            skLineSegment(sketch, "E8.0.8.1", {"start": v(0, -1464) * mm, "end": v(8000, -1464) * mm});
            skLineSegment(sketch, "E8.0.8.2", {"start": v(8000, -1304) * mm, "end": v(8000, -1464) * mm});
            skLineSegment(sketch, "E8.0.8.3", {"start": v(0, -1304) * mm, "end": v(0, -1464) * mm});
            skLineSegment(sketch, "E8.0.9.0", {"start": v(0, -1467) * mm, "end": v(8000, -1467) * mm});
            skLineSegment(sketch, "E8.0.9.1", {"start": v(0, -1627) * mm, "end": v(8000, -1627) * mm});
            skLineSegment(sketch, "E8.0.9.2", {"start": v(8000, -1467) * mm, "end": v(8000, -1627) * mm});
            skLineSegment(sketch, "E8.0.9.3", {"start": v(0, -1467) * mm, "end": v(0, -1627) * mm});
            skLineSegment(sketch, "E8.0.10.0", {"start": v(0, -1630) * mm, "end": v(8000, -1630) * mm});
            skLineSegment(sketch, "E8.0.10.1", {"start": v(0, -1790) * mm, "end": v(8000, -1790) * mm});
            skLineSegment(sketch, "E8.0.10.2", {"start": v(8000, -1630) * mm, "end": v(8000, -1790) * mm});
            skLineSegment(sketch, "E8.0.10.3", {"start": v(0, -1630) * mm, "end": v(0, -1790) * mm});
            skLineSegment(sketch, "E8.0.11.0", {"start": v(0, -1793) * mm, "end": v(8000, -1793) * mm});
            skLineSegment(sketch, "E8.0.11.1", {"start": v(0, -1953) * mm, "end": v(8000, -1953) * mm});
            skLineSegment(sketch, "E8.0.11.2", {"start": v(8000, -1793) * mm, "end": v(8000, -1953) * mm});
            skLineSegment(sketch, "E8.0.11.3", {"start": v(0, -1793) * mm, "end": v(0, -1953) * mm});
            skLineSegment(sketch, "E8.0.12.0", {"start": v(0, -1956) * mm, "end": v(8000, -1956) * mm});
            skLineSegment(sketch, "E8.0.12.1", {"start": v(0, -2116) * mm, "end": v(8000, -2116) * mm});
            skLineSegment(sketch, "E8.0.12.2", {"start": v(8000, -1956) * mm, "end": v(8000, -2116) * mm});
            skLineSegment(sketch, "E8.0.12.3", {"start": v(0, -1956) * mm, "end": v(0, -2116) * mm});
            skLineSegment(sketch, "E8.0.13.0", {"start": v(0, -2119) * mm, "end": v(8000, -2119) * mm});
            skLineSegment(sketch, "E8.0.13.1", {"start": v(0, -2279) * mm, "end": v(8000, -2279) * mm});
            skLineSegment(sketch, "E8.0.13.2", {"start": v(8000, -2119) * mm, "end": v(8000, -2279) * mm});
            skLineSegment(sketch, "E8.0.13.3", {"start": v(0, -2119) * mm, "end": v(0, -2279) * mm});
            skLineSegment(sketch, "E8.0.14.0", {"start": v(0, -2282) * mm, "end": v(8000, -2282) * mm});
            skLineSegment(sketch, "E8.0.14.1", {"start": v(0, -2442) * mm, "end": v(8000, -2442) * mm});
            skLineSegment(sketch, "E8.0.14.2", {"start": v(8000, -2282) * mm, "end": v(8000, -2442) * mm});
            skLineSegment(sketch, "E8.0.14.3", {"start": v(0, -2282) * mm, "end": v(0, -2442) * mm});
            skLineSegment(sketch, "E8.0.15.0", {"start": v(0, -2445) * mm, "end": v(8000, -2445) * mm});
            skLineSegment(sketch, "E8.0.15.1", {"start": v(0, -2605) * mm, "end": v(8000, -2605) * mm});
            skLineSegment(sketch, "E8.0.15.2", {"start": v(8000, -2445) * mm, "end": v(8000, -2605) * mm});
            skLineSegment(sketch, "E8.0.15.3", {"start": v(0, -2445) * mm, "end": v(0, -2605) * mm});
            skLineSegment(sketch, "E8.0.16.0", {"start": v(0, -2608) * mm, "end": v(8000, -2608) * mm});
            skLineSegment(sketch, "E8.0.16.1", {"start": v(0, -2768) * mm, "end": v(8000, -2768) * mm});
            skLineSegment(sketch, "E8.0.16.2", {"start": v(8000, -2608) * mm, "end": v(8000, -2768) * mm});
            skLineSegment(sketch, "E8.0.16.3", {"start": v(0, -2608) * mm, "end": v(0, -2768) * mm});
            skLineSegment(sketch, "E8.0.17.0", {"start": v(0, -2771) * mm, "end": v(8000, -2771) * mm});
            skLineSegment(sketch, "E8.0.17.1", {"start": v(0, -2931) * mm, "end": v(8000, -2931) * mm});
            skLineSegment(sketch, "E8.0.17.2", {"start": v(8000, -2771) * mm, "end": v(8000, -2931) * mm});
            skLineSegment(sketch, "E8.0.17.3", {"start": v(0, -2771) * mm, "end": v(0, -2931) * mm});
            skLineSegment(sketch, "E8.0.18.0", {"start": v(0, -2934) * mm, "end": v(8000, -2934) * mm});
            skLineSegment(sketch, "E8.0.18.1", {"start": v(0, -3094) * mm, "end": v(8000, -3094) * mm});
            skLineSegment(sketch, "E8.0.18.2", {"start": v(8000, -2934) * mm, "end": v(8000, -3094) * mm});
            skLineSegment(sketch, "E8.0.18.3", {"start": v(0, -2934) * mm, "end": v(0, -3094) * mm});
            skLineSegment(sketch, "E8.0.19.0", {"start": v(0, -3097) * mm, "end": v(8000, -3097) * mm});
            skLineSegment(sketch, "E8.0.19.1", {"start": v(0, -3257) * mm, "end": v(8000, -3257) * mm});
            skLineSegment(sketch, "E8.0.19.2", {"start": v(8000, -3097) * mm, "end": v(8000, -3257) * mm});
            skLineSegment(sketch, "E8.0.19.3", {"start": v(0, -3097) * mm, "end": v(0, -3257) * mm});
            skLineSegment(sketch, "E8.0.20.0", {"start": v(0, -3260) * mm, "end": v(8000, -3260) * mm});
            skLineSegment(sketch, "E8.0.20.1", {"start": v(0, -3420) * mm, "end": v(8000, -3420) * mm});
            skLineSegment(sketch, "E8.0.20.2", {"start": v(8000, -3260) * mm, "end": v(8000, -3420) * mm});
            skLineSegment(sketch, "E8.0.20.3", {"start": v(0, -3260) * mm, "end": v(0, -3420) * mm});
            skLineSegment(sketch, "E8.0.21.0", {"start": v(0, -3423) * mm, "end": v(8000, -3423) * mm});
            skLineSegment(sketch, "E8.0.21.1", {"start": v(0, -3583) * mm, "end": v(8000, -3583) * mm});
            skLineSegment(sketch, "E8.0.21.2", {"start": v(8000, -3423) * mm, "end": v(8000, -3583) * mm});
            skLineSegment(sketch, "E8.0.21.3", {"start": v(0, -3423) * mm, "end": v(0, -3583) * mm});
            skLineSegment(sketch, "E8.0.22.0", {"start": v(0, -3586) * mm, "end": v(8000, -3586) * mm});
            skLineSegment(sketch, "E8.0.22.1", {"start": v(0, -3746) * mm, "end": v(8000, -3746) * mm});
            skLineSegment(sketch, "E8.0.22.2", {"start": v(8000, -3586) * mm, "end": v(8000, -3746) * mm});
            skLineSegment(sketch, "E8.0.22.3", {"start": v(0, -3586) * mm, "end": v(0, -3746) * mm});
            skLineSegment(sketch, "E8.0.23.0", {"start": v(0, -3749) * mm, "end": v(8000, -3749) * mm});
            skLineSegment(sketch, "E8.0.23.1", {"start": v(0, -3909) * mm, "end": v(8000, -3909) * mm});
            skLineSegment(sketch, "E8.0.23.2", {"start": v(8000, -3749) * mm, "end": v(8000, -3909) * mm});
            skLineSegment(sketch, "E8.0.23.3", {"start": v(0, -3749) * mm, "end": v(0, -3909) * mm});
            skLineSegment(sketch, "E8.0.24.0", {"start": v(0, -3912) * mm, "end": v(8000, -3912) * mm});
            skLineSegment(sketch, "E8.0.24.1", {"start": v(0, -4072) * mm, "end": v(8000, -4072) * mm});
            skLineSegment(sketch, "E8.0.24.2", {"start": v(8000, -3912) * mm, "end": v(8000, -4072) * mm});
            skLineSegment(sketch, "E8.0.24.3", {"start": v(0, -3912) * mm, "end": v(0, -4072) * mm});
            skLineSegment(sketch, "E8.0.25.0", {"start": v(0, -4075) * mm, "end": v(8000, -4075) * mm});
            skLineSegment(sketch, "E8.0.25.1", {"start": v(0, -4235) * mm, "end": v(8000, -4235) * mm});
            skLineSegment(sketch, "E8.0.25.2", {"start": v(8000, -4075) * mm, "end": v(8000, -4235) * mm});
            skLineSegment(sketch, "E8.0.25.3", {"start": v(0, -4075) * mm, "end": v(0, -4235) * mm});
            skLineSegment(sketch, "E8.0.26.0", {"start": v(0, -4238) * mm, "end": v(8000, -4238) * mm});
            skLineSegment(sketch, "E8.0.26.1", {"start": v(0, -4398) * mm, "end": v(8000, -4398) * mm});
            skLineSegment(sketch, "E8.0.26.2", {"start": v(8000, -4238) * mm, "end": v(8000, -4398) * mm});
            skLineSegment(sketch, "E8.0.26.3", {"start": v(0, -4238) * mm, "end": v(0, -4398) * mm});
            skLineSegment(sketch, "E8.0.27.0", {"start": v(0, -4401) * mm, "end": v(8000, -4401) * mm});
            skLineSegment(sketch, "E8.0.27.1", {"start": v(0, -4561) * mm, "end": v(8000, -4561) * mm});
            skLineSegment(sketch, "E8.0.27.2", {"start": v(8000, -4401) * mm, "end": v(8000, -4561) * mm});
            skLineSegment(sketch, "E8.0.27.3", {"start": v(0, -4401) * mm, "end": v(0, -4561) * mm});
            skLineSegment(sketch, "E8.0.28.0", {"start": v(0, -4564) * mm, "end": v(8000, -4564) * mm});
            skLineSegment(sketch, "E8.0.28.1", {"start": v(0, -4724) * mm, "end": v(8000, -4724) * mm});
            skLineSegment(sketch, "E8.0.28.2", {"start": v(8000, -4564) * mm, "end": v(8000, -4724) * mm});
            skLineSegment(sketch, "E8.0.28.3", {"start": v(0, -4564) * mm, "end": v(0, -4724) * mm});
            skLineSegment(sketch, "E8.0.29.0", {"start": v(0, -4727) * mm, "end": v(8000, -4727) * mm});
            skLineSegment(sketch, "E8.0.29.1", {"start": v(0, -4887) * mm, "end": v(8000, -4887) * mm});
            skLineSegment(sketch, "E8.0.29.2", {"start": v(8000, -4727) * mm, "end": v(8000, -4887) * mm});
            skLineSegment(sketch, "E8.0.29.3", {"start": v(0, -4727) * mm, "end": v(0, -4887) * mm});
            skLineSegment(sketch, "E8.0.30.0", {"start": v(0, -4890) * mm, "end": v(8000, -4890) * mm});
            skLineSegment(sketch, "E8.0.30.1", {"start": v(0, -5050) * mm, "end": v(8000, -5050) * mm});
            skLineSegment(sketch, "E8.0.30.2", {"start": v(8000, -4890) * mm, "end": v(8000, -5050) * mm});
            skLineSegment(sketch, "E8.0.30.3", {"start": v(0, -4890) * mm, "end": v(0, -5050) * mm});
            skLineSegment(sketch, "E8.0.31.0", {"start": v(0, -5053) * mm, "end": v(8000, -5053) * mm});
            skLineSegment(sketch, "E8.0.31.1", {"start": v(0, -5213) * mm, "end": v(8000, -5213) * mm});
            skLineSegment(sketch, "E8.0.31.2", {"start": v(8000, -5053) * mm, "end": v(8000, -5213) * mm});
            skLineSegment(sketch, "E8.0.31.3", {"start": v(0, -5053) * mm, "end": v(0, -5213) * mm});
            skLineSegment(sketch, "E8.0.32.0", {"start": v(0, -5216) * mm, "end": v(8000, -5216) * mm});
            skLineSegment(sketch, "E8.0.32.1", {"start": v(0, -5376) * mm, "end": v(8000, -5376) * mm});
            skLineSegment(sketch, "E8.0.32.2", {"start": v(8000, -5216) * mm, "end": v(8000, -5376) * mm});
            skLineSegment(sketch, "E8.0.32.3", {"start": v(0, -5216) * mm, "end": v(0, -5376) * mm});
            skLineSegment(sketch, "E8.0.33.0", {"start": v(0, -5379) * mm, "end": v(8000, -5379) * mm});
            skLineSegment(sketch, "E8.0.33.1", {"start": v(0, -5539) * mm, "end": v(8000, -5539) * mm});
            skLineSegment(sketch, "E8.0.33.2", {"start": v(8000, -5379) * mm, "end": v(8000, -5539) * mm});
            skLineSegment(sketch, "E8.0.33.3", {"start": v(0, -5379) * mm, "end": v(0, -5539) * mm});
            skLineSegment(sketch, "E8.0.34.0", {"start": v(0, -5542) * mm, "end": v(8000, -5542) * mm});
            skLineSegment(sketch, "E8.0.34.1", {"start": v(0, -5702) * mm, "end": v(8000, -5702) * mm});
            skLineSegment(sketch, "E8.0.34.2", {"start": v(8000, -5542) * mm, "end": v(8000, -5702) * mm});
            skLineSegment(sketch, "E8.0.34.3", {"start": v(0, -5542) * mm, "end": v(0, -5702) * mm});
            skLineSegment(sketch, "E8.0.35.0", {"start": v(0, -5705) * mm, "end": v(8000, -5705) * mm});
            skLineSegment(sketch, "E8.0.35.1", {"start": v(0, -5865) * mm, "end": v(8000, -5865) * mm});
            skLineSegment(sketch, "E8.0.35.2", {"start": v(8000, -5705) * mm, "end": v(8000, -5865) * mm});
            skLineSegment(sketch, "E8.0.35.3", {"start": v(0, -5705) * mm, "end": v(0, -5865) * mm});
            skLineSegment(sketch, "E8.0.36.0", {"start": v(0, -5868) * mm, "end": v(8000, -5868) * mm});
            skLineSegment(sketch, "E8.0.36.1", {"start": v(0, -6028) * mm, "end": v(8000, -6028) * mm});
            skLineSegment(sketch, "E8.0.36.2", {"start": v(8000, -5868) * mm, "end": v(8000, -6028) * mm});
            skLineSegment(sketch, "E8.0.36.3", {"start": v(0, -5868) * mm, "end": v(0, -6028) * mm});
            skLineSegment(sketch, "E8.direction1", {"start": v(0, -160) * mm, "end": v(25, -160) * mm, "construction": true});
            skLineSegment(sketch, "E8.direction2", {"start": v(0, -160) * mm, "end": v(0, -323) * mm, "construction": true});
            skLineSegment(sketch, "E9.0.0.37", {"start": v(0, -6031) * mm, "end": v(8000, -6031) * mm});
            skLineSegment(sketch, "E9.3.0.37", {"start": v(0, -6191) * mm, "end": v(8000, -6191) * mm});
            skLineSegment(sketch, "E9.6.0.37", {"start": v(8000, -6031) * mm, "end": v(8000, -6191) * mm});
            skLineSegment(sketch, "E9.9.0.37", {"start": v(0, -6031) * mm, "end": v(0, -6191) * mm});
            skLineSegment(sketch, "E9.0.0.38", {"start": v(0, -6194) * mm, "end": v(8000, -6194) * mm});
            skLineSegment(sketch, "E9.3.0.38", {"start": v(0, -6354) * mm, "end": v(8000, -6354) * mm});
            skLineSegment(sketch, "E9.6.0.38", {"start": v(8000, -6194) * mm, "end": v(8000, -6354) * mm});
            skLineSegment(sketch, "E9.9.0.38", {"start": v(0, -6194) * mm, "end": v(0, -6354) * mm});
            skLineSegment(sketch, "E9.0.0.39", {"start": v(0, -6357) * mm, "end": v(8000, -6357) * mm});
            skLineSegment(sketch, "E9.3.0.39", {"start": v(0, -6517) * mm, "end": v(8000, -6517) * mm});
            skLineSegment(sketch, "E9.6.0.39", {"start": v(8000, -6357) * mm, "end": v(8000, -6517) * mm});
            skLineSegment(sketch, "E9.9.0.39", {"start": v(0, -6357) * mm, "end": v(0, -6517) * mm});
            skLineSegment(sketch, "E9.0.0.40", {"start": v(0, -6520) * mm, "end": v(8000, -6520) * mm});
            skLineSegment(sketch, "E9.3.0.40", {"start": v(0, -6680) * mm, "end": v(8000, -6680) * mm});
            skLineSegment(sketch, "E9.6.0.40", {"start": v(8000, -6520) * mm, "end": v(8000, -6680) * mm});
            skLineSegment(sketch, "E9.9.0.40", {"start": v(0, -6520) * mm, "end": v(0, -6680) * mm});
            skLineSegment(sketch, "E9.0.0.41", {"start": v(0, -6683) * mm, "end": v(8000, -6683) * mm});
            skLineSegment(sketch, "E9.3.0.41", {"start": v(0, -6843) * mm, "end": v(8000, -6843) * mm});
            skLineSegment(sketch, "E9.6.0.41", {"start": v(8000, -6683) * mm, "end": v(8000, -6843) * mm});
            skLineSegment(sketch, "E9.9.0.41", {"start": v(0, -6683) * mm, "end": v(0, -6843) * mm});
            skLineSegment(sketch, "E9.0.0.42", {"start": v(0, -6846) * mm, "end": v(8000, -6846) * mm});
            skLineSegment(sketch, "E9.3.0.42", {"start": v(0, -7006) * mm, "end": v(8000, -7006) * mm});
            skLineSegment(sketch, "E9.6.0.42", {"start": v(8000, -6846) * mm, "end": v(8000, -7006) * mm});
            skLineSegment(sketch, "E9.9.0.42", {"start": v(0, -6846) * mm, "end": v(0, -7006) * mm});
            skLineSegment(sketch, "E9.0.0.43", {"start": v(0, -7009) * mm, "end": v(8000, -7009) * mm});
            skLineSegment(sketch, "E9.3.0.43", {"start": v(0, -7169) * mm, "end": v(8000, -7169) * mm});
            skLineSegment(sketch, "E9.6.0.43", {"start": v(8000, -7009) * mm, "end": v(8000, -7169) * mm});
            skLineSegment(sketch, "E9.9.0.43", {"start": v(0, -7009) * mm, "end": v(0, -7169) * mm});
            skLineSegment(sketch, "E9.0.0.44", {"start": v(0, -7172) * mm, "end": v(8000, -7172) * mm});
            skLineSegment(sketch, "E9.3.0.44", {"start": v(0, -7332) * mm, "end": v(8000, -7332) * mm});
            skLineSegment(sketch, "E9.6.0.44", {"start": v(8000, -7172) * mm, "end": v(8000, -7332) * mm});
            skLineSegment(sketch, "E9.9.0.44", {"start": v(0, -7172) * mm, "end": v(0, -7332) * mm});
            skLineSegment(sketch, "E10.0.0.45", {"start": v(0, -7335) * mm, "end": v(8000, -7335) * mm});
            skLineSegment(sketch, "E10.3.0.45", {"start": v(0, -7495) * mm, "end": v(8000, -7495) * mm});
            skLineSegment(sketch, "E10.6.0.45", {"start": v(8000, -7335) * mm, "end": v(8000, -7495) * mm});
            skLineSegment(sketch, "E10.9.0.45", {"start": v(0, -7335) * mm, "end": v(0, -7495) * mm});
            skLineSegment(sketch, "E10.0.0.46", {"start": v(0, -7498) * mm, "end": v(8000, -7498) * mm});
            skLineSegment(sketch, "E10.3.0.46", {"start": v(0, -7658) * mm, "end": v(8000, -7658) * mm});
            skLineSegment(sketch, "E10.6.0.46", {"start": v(8000, -7498) * mm, "end": v(8000, -7658) * mm});
            skLineSegment(sketch, "E10.9.0.46", {"start": v(0, -7498) * mm, "end": v(0, -7658) * mm});
            skLineSegment(sketch, "E10.0.0.47", {"start": v(0, -7661) * mm, "end": v(8000, -7661) * mm});
            skLineSegment(sketch, "E10.3.0.47", {"start": v(0, -7821) * mm, "end": v(8000, -7821) * mm});
            skLineSegment(sketch, "E10.6.0.47", {"start": v(8000, -7661) * mm, "end": v(8000, -7821) * mm});
            skLineSegment(sketch, "E10.9.0.47", {"start": v(0, -7661) * mm, "end": v(0, -7821) * mm});
            skLineSegment(sketch, "E10.0.0.48", {"start": v(0, -7824) * mm, "end": v(8000, -7824) * mm});
            skLineSegment(sketch, "E10.3.0.48", {"start": v(0, -7984) * mm, "end": v(8000, -7984) * mm});
            skLineSegment(sketch, "E10.6.0.48", {"start": v(8000, -7824) * mm, "end": v(8000, -7984) * mm});
            skLineSegment(sketch, "E10.9.0.48", {"start": v(0, -7824) * mm, "end": v(0, -7984) * mm});
            skSolve(sketch);
        }
        {
            var Q0;
            Q0 = qSketchRegion(id + "F2", true);
            extrude(context, id + "F3", {"entities" : qUnion([Q0]), "operationType" : NewBodyOperationType.ADD, "depth" : 25 * mm});
        }
    });
